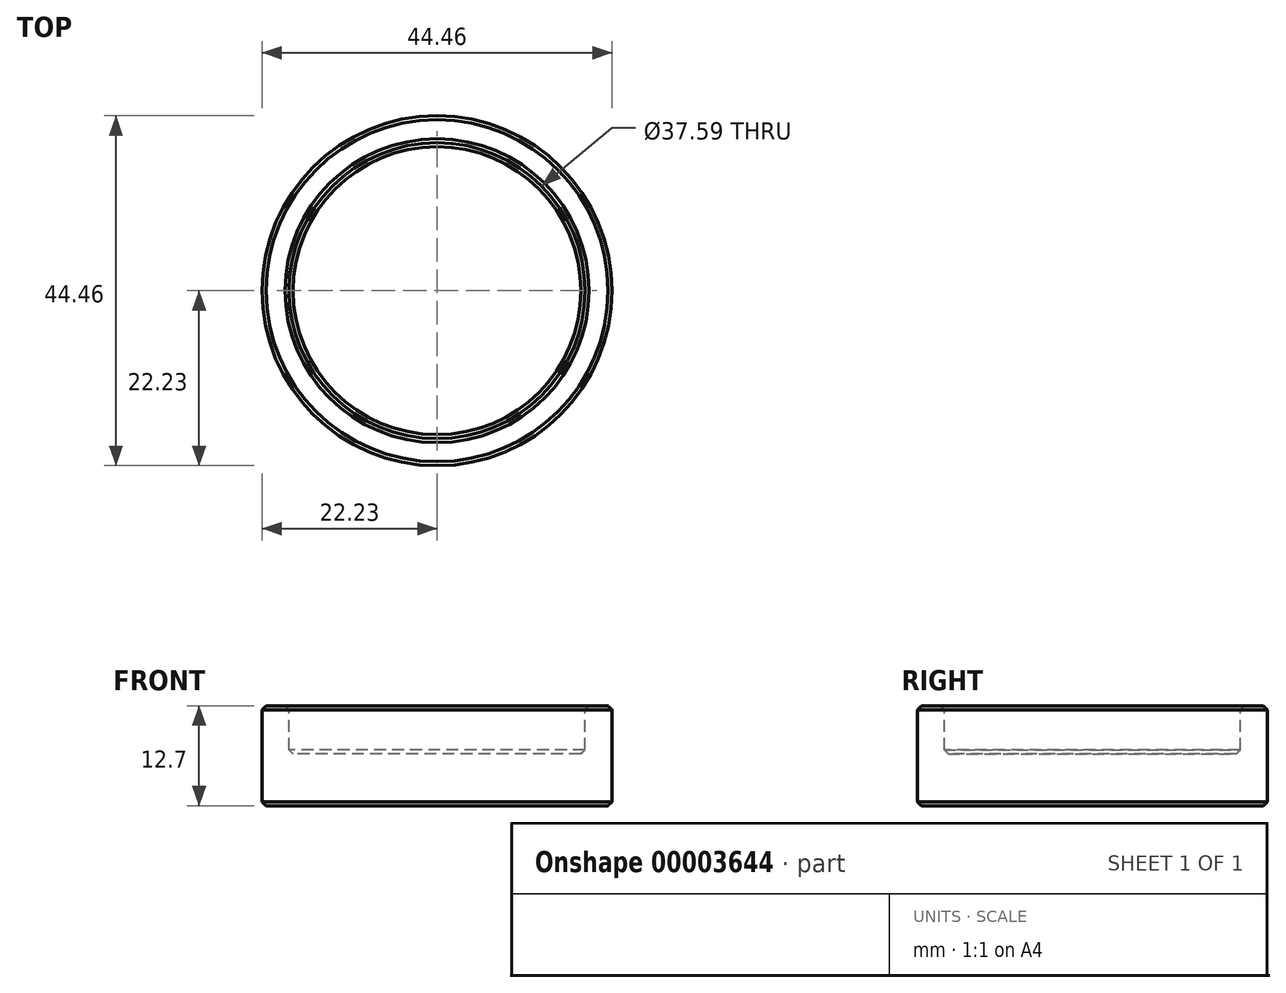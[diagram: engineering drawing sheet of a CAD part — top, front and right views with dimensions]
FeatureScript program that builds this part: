
annotation { "Feature Type Name" : "Feature", "Feature Type Description" : "" }
export const myFeature = defineFeature(function(context is Context, id is Id, definition is map)
    precondition{}
    {
        {
            var Q0;
            Q0=qCreatedBy(makeId("Top.planeOp"),FACE);
            var sketch = newSketch(context, id + "F0", { "sketchPlane" : qUnion([Q0])});
            skCircle(sketch, "E0", {"center": v(0, 0) * mm, "radius": 22.23 * mm});
            skSolve(sketch);
        }
        {
            var Q0;
            Q0 = qSketchRegion(id + "F0", true);
            extrude(context, id + "F1", {"entities" : qUnion([Q0]), "oppositeDirection" : true, "depth" : 12.7 * mm});
        }
        {
            var Q0;
            Q0=makeQuery(id+"F1.opExtrude","CAP_FACE",FACE,{"disambiguationData":[OSD([sQuery(id+"F0.wireOp",EDGE,"E0")])],"isStart":true});
            var sketch = newSketch(context, id + "F2", { "sketchPlane" : qUnion([Q0])});
            skCircle(sketch, "E1", {"center": v(0, 0) * mm, "radius": 18.8 * mm});
            skSolve(sketch);
        }
        {
            var Q0;
            Q0 = qSketchRegion(id + "F2", true);
            extrude(context, id + "F3", {"entities" : qUnion([Q0]), "operationType" : NewBodyOperationType.REMOVE, "oppositeDirection" : true, "depth" : 6.1 * mm});
        }
        {
            var Q0;
            Q0=makeQuery(id+"F3.boolean.opBoolean","COPY",EDGE,{"derivedFrom":makeQuery(id+"F3.opExtrude","CAP_EDGE",EDGE,{"disambiguationData":[OSD([sQuery(id+"F2.wireOp",EDGE,"E1")])],"isStart":false})});
            var Q1;
            Q1=makeQuery(id+"F1.opExtrude","CAP_FACE",FACE,{"disambiguationData":[OSD([sQuery(id+"F0.wireOp",EDGE,"E0")])],"isStart":true});
            var Q2;
            Q2=makeQuery(id+"F1.opExtrude","CAP_FACE",FACE,{"disambiguationData":[OSD([sQuery(id+"F0.wireOp",EDGE,"E0")])],"isStart":false});
            chamfer(context, id + "F4", {"entities" : qUnion([Q0, Q1, Q2]), "chamferType" : ChamferType.OFFSET_ANGLE, "width" : 0.5 * mm, "oppositeDirection" : false, "angle" : 45 * degree, "tangentPropagation" : true});
        }
    });
